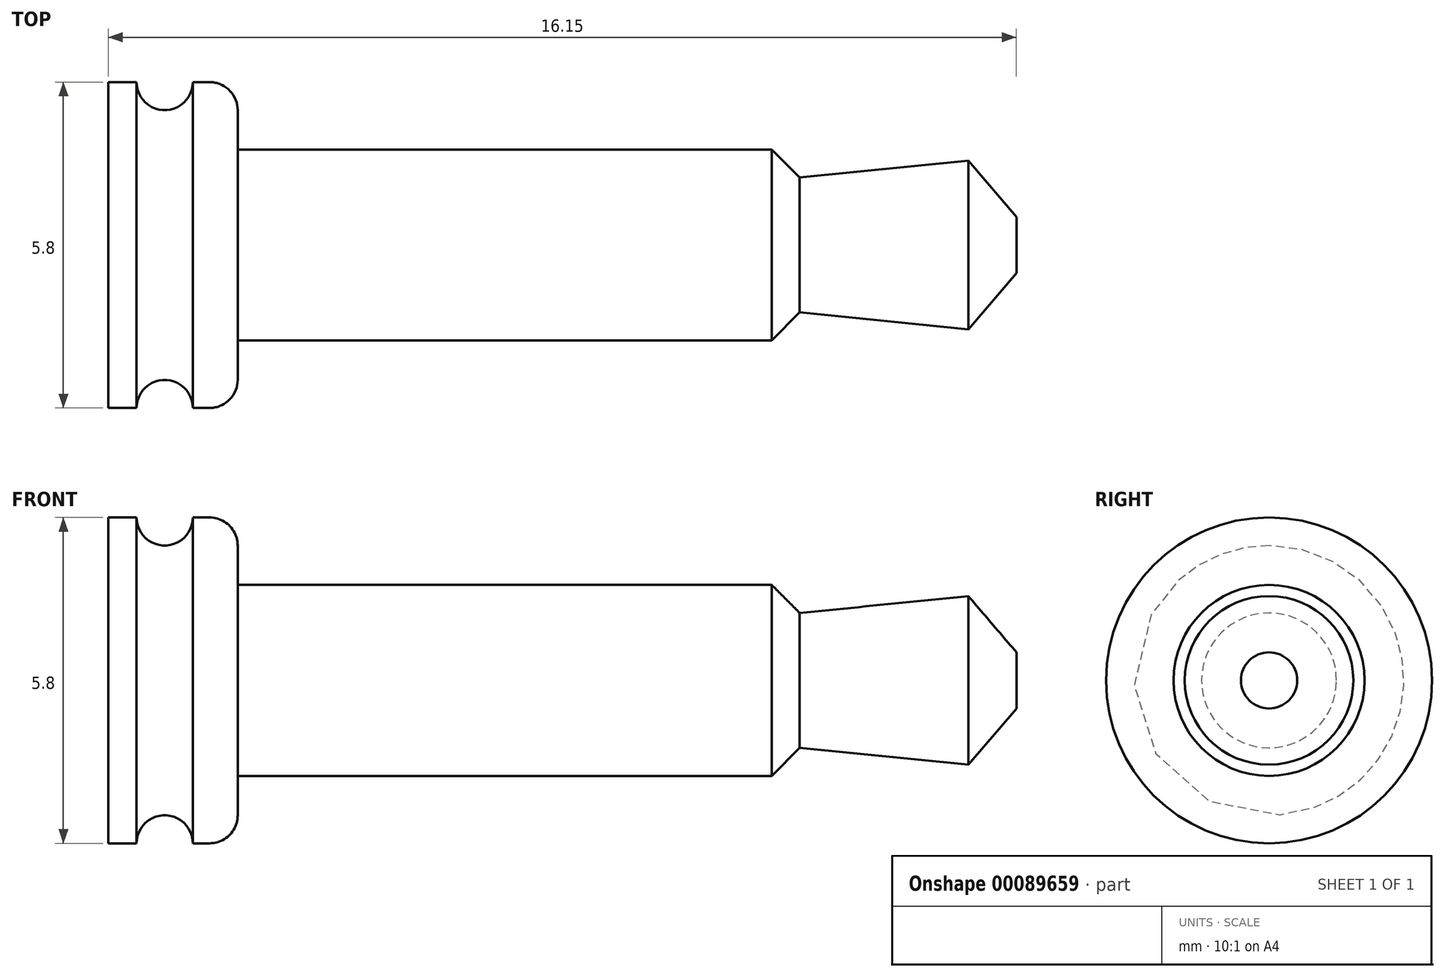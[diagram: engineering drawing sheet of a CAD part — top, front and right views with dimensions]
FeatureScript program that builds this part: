
annotation { "Feature Type Name" : "Feature", "Feature Type Description" : "" }
export const myFeature = defineFeature(function(context is Context, id is Id, definition is map)
    precondition{}
    {
        {
            var Q0;
            Q0=qCreatedBy(makeId("Front.planeOp"),FACE);
            var sketch = newSketch(context, id + "F0", { "sketchPlane" : qUnion([Q0])});
            skLineSegment(sketch, "E0", {"start": v(0, 0) * mm, "end": v(0, -2.9) * mm});
            skLineSegment(sketch, "E1", {"start": v(0, -2.9) * mm, "end": v(0.5, -2.9) * mm});
            skPoint(sketch, "E2.end.orphan", {"position": v(21.46, 0) * mm});
            skArc(sketch, "E3", {"start": v(1.5, -2.9) * mm, "mid": v(1, -2.4) * mm, "end": v(0.5, -2.9) * mm});
            skLineSegment(sketch, "E4", {"start": v(1.5, -2.9) * mm, "end": v(1.8, -2.9) * mm});
            skLineSegment(sketch, "E5", {"start": v(2.3, -2.4) * mm, "end": v(2.3, -1.7) * mm});
            skLineSegment(sketch, "E6", {"start": v(2.3, -1.7) * mm, "end": v(11.8, -1.7) * mm});
            skLineSegment(sketch, "E7", {"start": v(11.8, -1.7) * mm, "end": v(12.3, -1.2) * mm});
            skLineSegment(sketch, "E8", {"start": v(12.3, -1.2) * mm, "end": v(15.3, -1.5) * mm});
            skLineSegment(sketch, "E9", {"start": v(15.3, -1.5) * mm, "end": v(16.15, -0.5) * mm});
            skLineSegment(sketch, "E10", {"start": v(16.15, -0.5) * mm, "end": v(16.15, 0) * mm});
            skLineSegment(sketch, "E11", {"start": v(16.15, 0) * mm, "end": v(0, 0) * mm});
            skPoint(sketch, "E12.visualSharp", {"position": v(2.3, -2.9) * mm});
            skArc(sketch, "E12.filletArc", {"start": v(1.8, -2.9) * mm, "mid": v(2.15, -2.75) * mm, "end": v(2.3, -2.4) * mm});
            skLineSegment(sketch, "E13", {"start": v(-6.74, 0) * mm, "end": v(28.4, 0) * mm});
            skSolve(sketch);
        }
        {
            var Q0;
            {var subQ0=sQuery(id+"F0.wireOp",EDGE,"E0");Q0=makeQuery(id+"F0.imprint","IMPRINT",FACE,{"disambiguationData":[TD([[makeQuery(id+"F0.imprint","IMPRINT",EDGE,{"derivedFrom":subQ0}),1.0]])]});}
            var Q1;
            Q1=sQuery(id+"F0.wireOp",EDGE,"E13");
            revolve(context, id + "F1", {"entities" : qUnion([Q0]), "axis" : qUnion([Q1]), "revolveType" : RevolveType.FULL});
        }
    });
